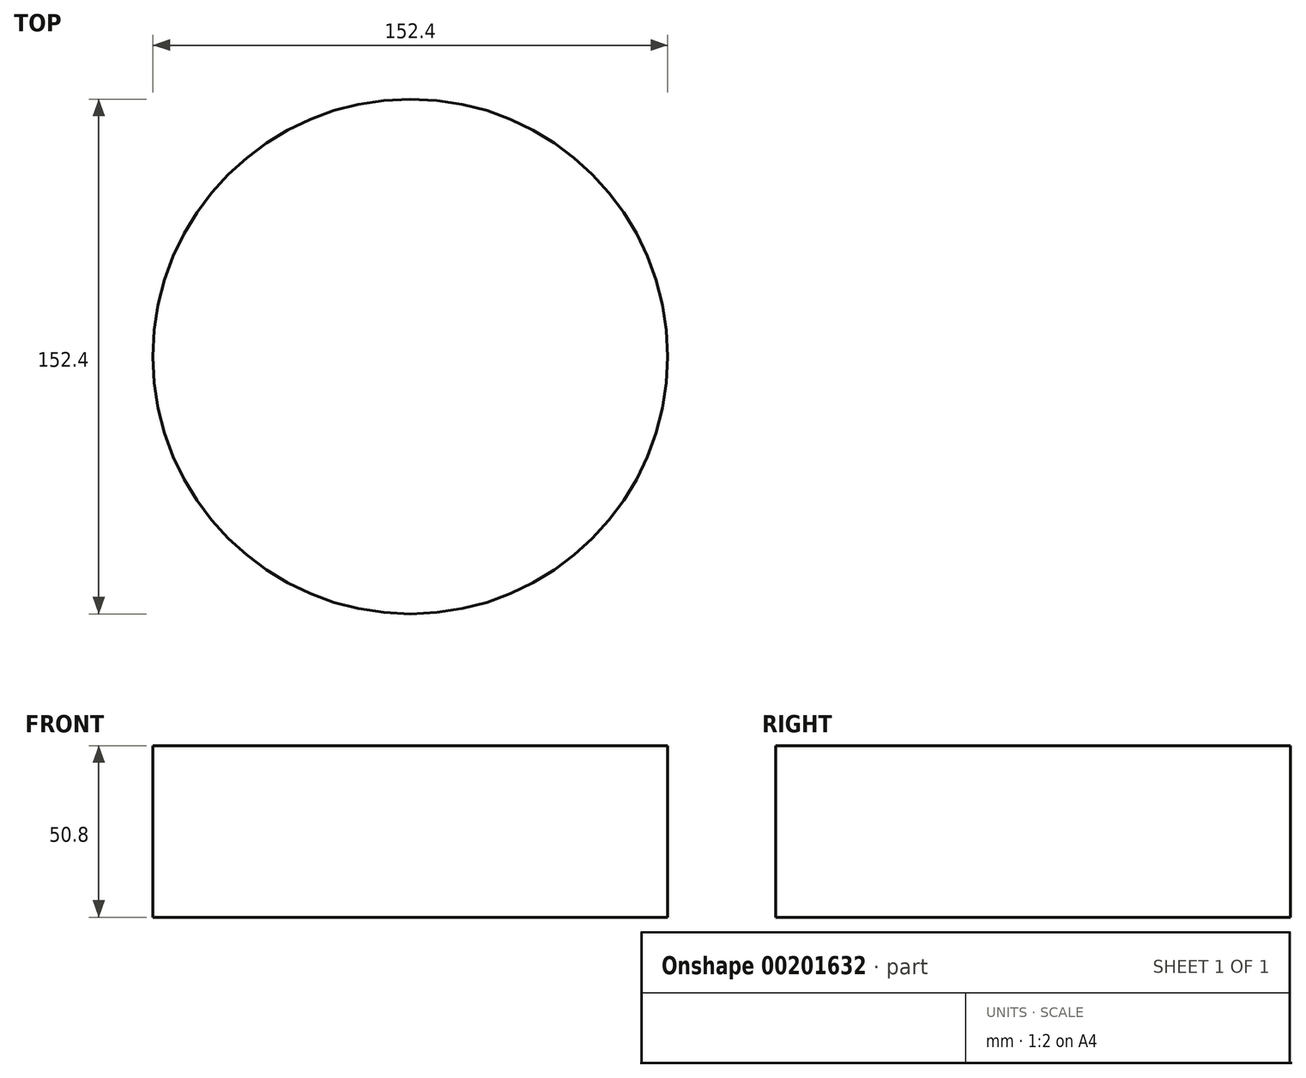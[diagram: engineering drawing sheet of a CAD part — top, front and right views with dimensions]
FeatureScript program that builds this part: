
annotation { "Feature Type Name" : "Feature", "Feature Type Description" : "" }
export const myFeature = defineFeature(function(context is Context, id is Id, definition is map)
    precondition{}
    {
        {
            var Q0;
            Q0=qCreatedBy(makeId("Top.planeOp"),FACE);
            var sketch = newSketch(context, id + "F0", { "sketchPlane" : qUnion([Q0])});
            skCircle(sketch, "E0", {"center": v(0, 0) * mm, "radius": 76.2 * mm});
            skSolve(sketch);
        }
        {
            var Q0;
            Q0 = qSketchRegion(id + "F0", true);
            extrude(context, id + "F1", {"entities" : qUnion([Q0]), "depth" : 50.8 * mm});
        }
    });
